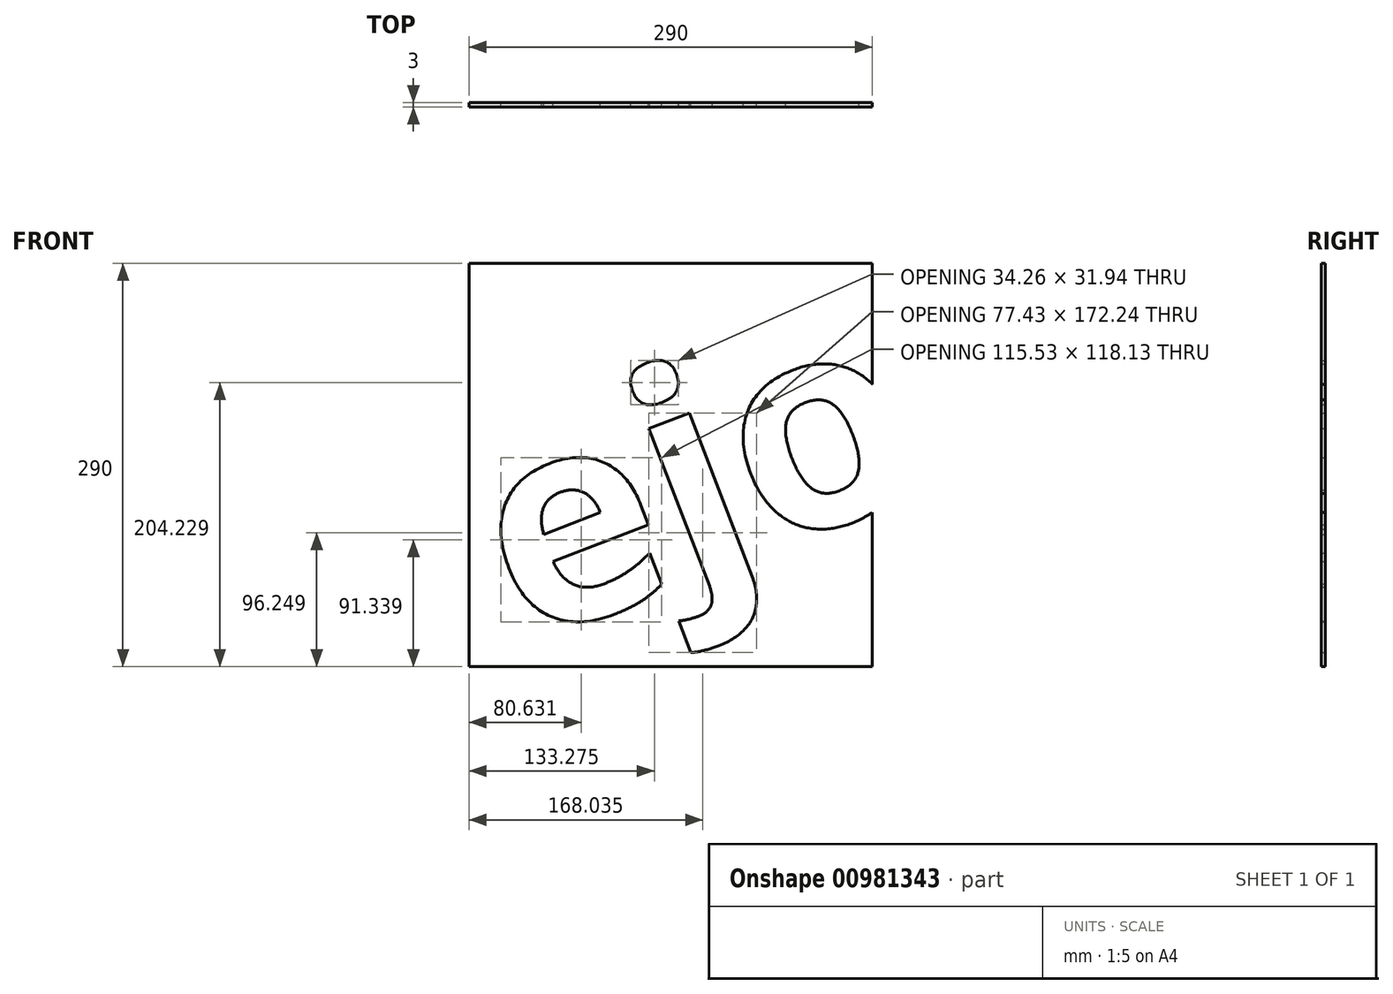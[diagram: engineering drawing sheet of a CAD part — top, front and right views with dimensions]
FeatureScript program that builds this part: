
annotation { "Feature Type Name" : "Feature", "Feature Type Description" : "" }
export const myFeature = defineFeature(function(context is Context, id is Id, definition is map)
    precondition{}
    {
        {
            var Q0;
            Q0=qCreatedBy(makeId("Front.planeOp"),FACE);
            var sketch = newSketch(context, id + "F0", { "sketchPlane" : qUnion([Q0])});
            skLineSegment(sketch, "E0.bottom", {"start": v(-133.06, 193.31) * mm, "end": v(156.94, 193.31) * mm});
            skLineSegment(sketch, "E0.top", {"start": v(-133.06, -96.69) * mm, "end": v(156.94, -96.69) * mm});
            skLineSegment(sketch, "E0.left", {"start": v(-133.06, 193.31) * mm, "end": v(-133.06, -96.69) * mm});
            skLineSegment(sketch, "E0.right", {"start": v(156.94, 193.31) * mm, "end": v(156.94, -96.69) * mm});
            skText(sketch, "E1", { "text": "ejo", "fontName": "OpenSans-Bold.ttf"});
            skLineSegment(sketch, "E2", {"start": v(-133.06, -188.62) * mm, "end": v(155.38, -77.9) * mm, "construction": true});
            skLineSegment(sketch, "E3", {"start": v(-133.06, -96.69) * mm, "end": v(-133.06, -188.62) * mm, "construction": true});
            skLineSegment(sketch, "E4", {"start": v(-89.48, 29.23) * mm, "end": v(-46.48, -82.8) * mm, "construction": true});
            skLineSegment(sketch, "E5", {"start": v(-118.8, -38.82) * mm, "end": v(161.28, 68.7) * mm, "construction": true});
            skPoint(sketch, "E6.visualSharp", {"position": v(-133.06, -96.69) * mm});
            const initialGuessF0  = {"E1": [-0.09308, -0.08156, 0.93358, 0.35837, 0.15]};
            skSetInitialGuess(sketch, initialGuessF0);
            skSolve(sketch);
        }
        {
            var Q0;
            {var subQ1=sQuery(id+"F0.wireOp",EDGE,"E0.bottom");Q0=makeQuery(id+"F0.imprint","IMPRINT",FACE,{"disambiguationData":[TD([[makeQuery(id+"F0.imprint","IMPRINT",EDGE,{"derivedFrom":subQ1}),-1.0]])]});}
            var Q1;
            Q1=makeQuery(id+"F0.imprint","IMPRINT",FACE,{"disambiguationData":[TD([[makeQuery(id+"F0.imprint","IMPRINT",EDGE,{"derivedFrom":sQuery(id+"F0.wireOp",EDGE,"E1.sketch_text.stroke-0")}),1.0]])]});
            var Q2;
            Q2=makeQuery(id+"F0.imprint","IMPRINT",FACE,{"disambiguationData":[TD([[makeQuery(id+"F0.imprint","IMPRINT",EDGE,{"derivedFrom":sQuery(id+"F0.wireOp",EDGE,"E1.sketch_text.stroke-35")}),1.0]])]});
            extrude(context, id + "F1", {"entities" : qUnion([Q0, Q1, Q2]), "depth" : 3 * mm, "offsetDistance" : 25 * mm});
        }
    });
